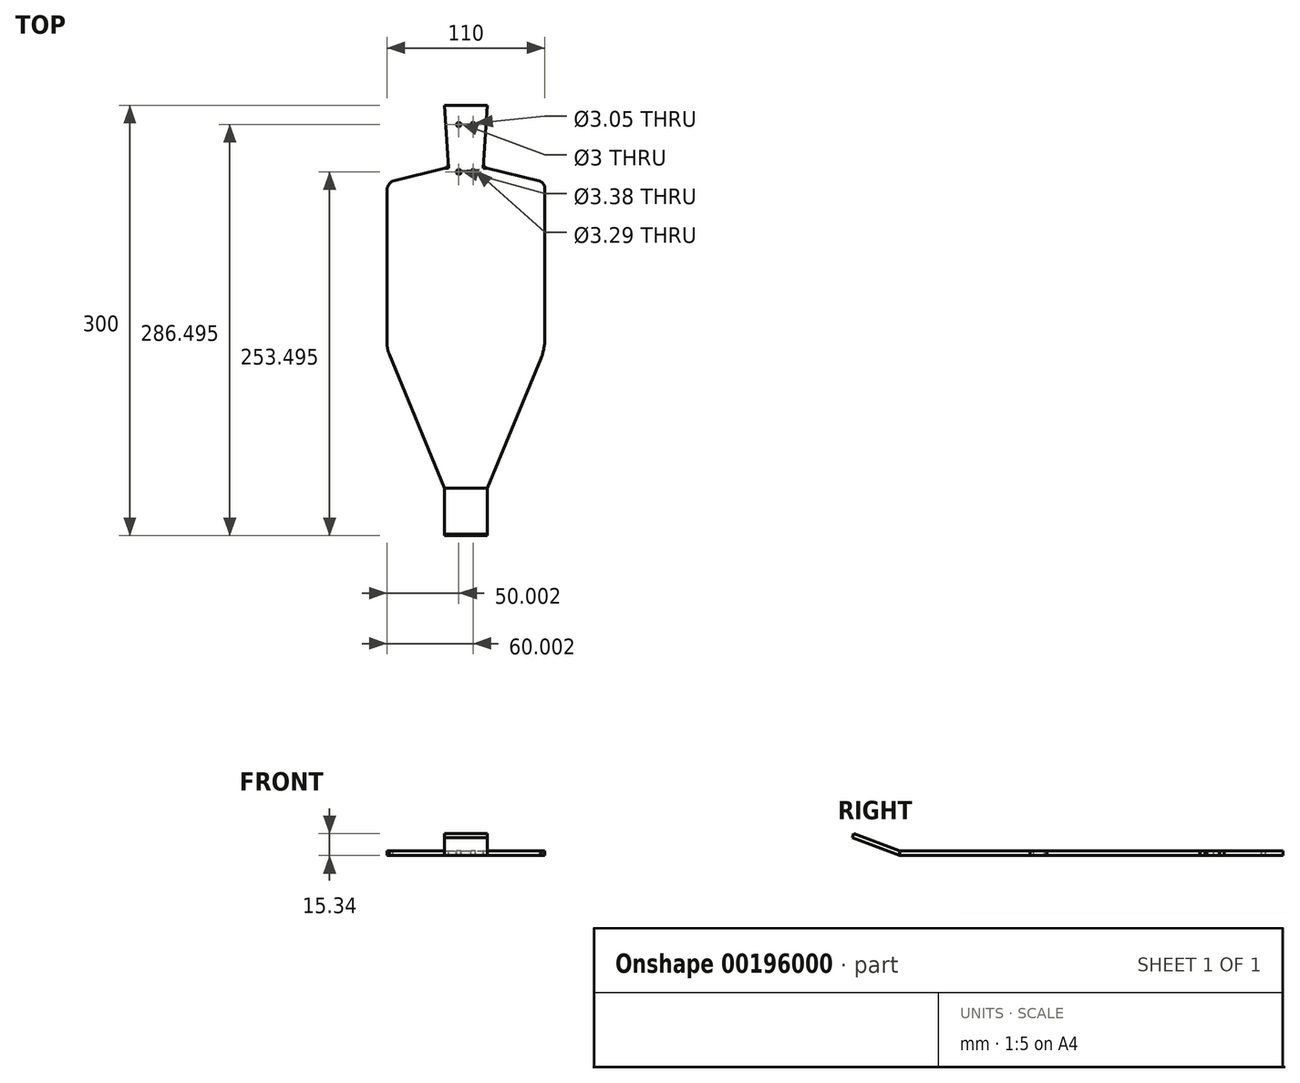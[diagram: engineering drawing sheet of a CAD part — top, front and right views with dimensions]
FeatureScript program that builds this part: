
annotation { "Feature Type Name" : "Feature", "Feature Type Description" : "" }
export const myFeature = defineFeature(function(context is Context, id is Id, definition is map)
    precondition{}
    {
        {
            var Q0;
            Q0=qCreatedBy(makeId("Top.planeOp"),FACE);
            var sketch = newSketch(context, id + "F0", { "sketchPlane" : qUnion([Q0])});
            skLineSegment(sketch, "E0.bottom", {"start": v(-49.3, 160.69) * mm, "end": v(-19.3, 160.69) * mm});
            skLineSegment(sketch, "E0.top", {"start": v(-49.3, -139.31) * mm, "end": v(-19.3, -139.31) * mm});
            skLineSegment(sketch, "E0.left", {"start": v(-49.3, -106.28) * mm, "end": v(-49.3, -139.31) * mm});
            skLineSegment(sketch, "E0.right", {"start": v(-19.3, -106.28) * mm, "end": v(-19.3, -139.31) * mm});
            skLineSegment(sketch, "E1", {"start": v(-49.3, 116.69) * mm, "end": v(-19.3, 116.69) * mm});
            skLineSegment(sketch, "E2", {"start": v(-19.3, 160.69) * mm, "end": v(-22.3, 116.69) * mm});
            skLineSegment(sketch, "E3", {"start": v(-46.3, 116.69) * mm, "end": v(-49.3, 116.69) * mm});
            skLineSegment(sketch, "E4", {"start": v(-49.3, 160.69) * mm, "end": v(-46.3, 116.69) * mm});
            skLineSegment(sketch, "E5", {"start": v(-49.3, 116.69) * mm, "end": v(-46.3, 116.69) * mm});
            skLineSegment(sketch, "E6", {"start": v(-49.3, 116.69) * mm, "end": v(-89.3, 106.83) * mm});
            skLineSegment(sketch, "E7", {"start": v(-19.3, 116.69) * mm, "end": v(20.7, 106.83) * mm});
            skLineSegment(sketch, "E8.left", {"start": v(-89.3, 106.83) * mm, "end": v(-89.3, -9.31) * mm});
            skLineSegment(sketch, "E8.right", {"start": v(20.7, 106.83) * mm, "end": v(20.7, -9.31) * mm});
            skLineSegment(sketch, "E9", {"start": v(-89.3, -9.31) * mm, "end": v(-49.3, -106.28) * mm});
            skLineSegment(sketch, "E10", {"start": v(-49.3, -106.28) * mm, "end": v(-19.3, -106.28) * mm});
            skLineSegment(sketch, "E11", {"start": v(-19.3, -106.28) * mm, "end": v(20.7, -9.31) * mm});
            skLineSegment(sketch, "E12.trimOffspring", {"start": v(-22.3, 116.69) * mm, "end": v(-19.3, 116.69) * mm});
            skPoint(sketch, "E13.orphan", {"position": v(-34.3, 160.69) * mm});
            skSolve(sketch);
        }
        {
            var Q0;
            Q0 = qSketchRegion(id + "F0", true);
            extrude(context, id + "F1", {"entities" : qUnion([Q0]), "depth" : 3.25 * mm});
        }
        {
            var Q0;
            Q0=makeQuery(id+"F0.imprint","IMPRINT",FACE,{"disambiguationData":[TD([[makeQuery(id+"F0.imprint","IMPRINT",EDGE,{"derivedFrom":sQuery(id+"F0.wireOp",EDGE,"E0.top")}),1.0]])]});
            extrude(context, id + "F2", {"entities" : qUnion([Q0]), "operationType" : NewBodyOperationType.ADD, "depth" : 25 * mm});
        }
        {
            var Q0;
            {var subQ0=sQuery(id+"F0.wireOp",EDGE,"E0.left");Q0=makeQuery(id+"F2.boolean.opBoolean","MERGE",FACE,{"derivedFrom":[makeQuery(id+"F1.opExtrude","SWEPT_FACE",FACE,{"disambiguationData":[OSD([subQ0])]}),makeQuery(id+"F2.opExtrude","SWEPT_FACE",FACE,{"disambiguationData":[OSD([subQ0])]})]});}
            var sketch = newSketch(context, id + "F3", { "sketchPlane" : qUnion([Q0])});
            skLineSegment(sketch, "E14", {"start": v(106.28, 3.25) * mm, "end": v(138.24, 15.34) * mm});
            skLineSegment(sketch, "E15", {"start": v(106.28, 0) * mm, "end": v(139.31, 12.5) * mm});
            skLineSegment(sketch, "E16", {"start": v(139.31, 12.5) * mm, "end": v(138.08, 15.75) * mm});
            skPoint(sketch, "E17.orphan", {"position": v(139.31, 15.75) * mm});
            skSolve(sketch);
        }
        {
            var Q0;
            Q0 = qSketchRegion(id + "F3", true);
            var Q1;
            {var subQ2=sQuery(id+"F3.wireOp",EDGE,"E14");Q1=makeQuery(id+"F3.imprint","IMPRINT",FACE,{"disambiguationData":[TD([[makeQuery(id+"F3.imprint","IMPRINT",EDGE,{"derivedFrom":subQ2}),1.0]])]});}
            var Q2;
            {var subQ0=sQuery(id+"F3.wireOp",EDGE,"E15");Q2=makeQuery(id+"F3.imprint","IMPRINT",FACE,{"disambiguationData":[TD([[makeQuery(id+"F3.imprint","IMPRINT",EDGE,{"derivedFrom":subQ0}),-1.0]])]});}
            extrude(context, id + "F4", {"entities" : qUnion([Q0, Q1, Q2]), "operationType" : NewBodyOperationType.REMOVE, "oppositeDirection" : true, "depth" : 70 * mm});
        }
        {
            var Q0;
            Q0=makeQuery(id+"F1.opExtrude","CAP_FACE",FACE,{"disambiguationData":[OSD([sQuery(id+"F0.wireOp",EDGE,"E0.bottom"),sQuery(id+"F0.wireOp",EDGE,"E0.top"),sQuery(id+"F0.wireOp",EDGE,"E0.left"),sQuery(id+"F0.wireOp",EDGE,"E0.right"),sQuery(id+"F0.wireOp",EDGE,"E2"),sQuery(id+"F0.wireOp",EDGE,"E4"),sQuery(id+"F0.wireOp",EDGE,"E5"),sQuery(id+"F0.wireOp",EDGE,"E6"),sQuery(id+"F0.wireOp",EDGE,"E7"),sQuery(id+"F0.wireOp",EDGE,"E8.left"),sQuery(id+"F0.wireOp",EDGE,"E8.right"),sQuery(id+"F0.wireOp",EDGE,"E9"),sQuery(id+"F0.wireOp",EDGE,"E11"),sQuery(id+"F0.wireOp",EDGE,"E12.trimOffspring")])],"isStart":false});
            var sketch = newSketch(context, id + "F5", { "sketchPlane" : qUnion([Q0])});
            skArc(sketch, "E18", {"start": v(-89.3, -3.58) * mm, "mid": v(-89.01, -8.32) * mm, "end": v(-87.81, -12.92) * mm});
            skArc(sketch, "E19", {"start": v(18.14, -15.52) * mm, "mid": v(19.8, -9.63) * mm, "end": v(20.7, -3.58) * mm});
            skSolve(sketch);
        }
        {
            var Q0;
            {var subQ0=sQuery(id+"F5.wireOp",EDGE,"E19");Q0=makeQuery(id+"F5.imprint","IMPRINT",FACE,{"disambiguationData":[TD([[makeQuery(id+"F5.imprint","IMPRINT",EDGE,{"derivedFrom":subQ0}),-1.0]])]});}
            var Q1;
            {var subQ0=sQuery(id+"F5.wireOp",EDGE,"E18");var subQ1=makeQuery(id+"F1.opExtrude","CAP_EDGE",EDGE,{"disambiguationData":[OSD([sQuery(id+"F0.wireOp",EDGE,"E9")])],"isStart":false});var subQ2=makeQuery(id+"F5.imprint","INTERSECT",VERTEX,{"derivedFrom":[subQ1,subQ0]});Q1=makeQuery(id+"F5.imprint","IMPRINT",FACE,{"disambiguationData":[TD([[makeQuery(id+"F5.imprint","IMPRINT",EDGE,{"disambiguationData":[TD([[subQ2,1.0]])],"derivedFrom":subQ0}),-1.0]])]});}
            extrude(context, id + "F6", {"entities" : qUnion([Q0, Q1]), "operationType" : NewBodyOperationType.REMOVE, "oppositeDirection" : true, "depth" : 25 * mm});
        }
        {
            var Q0;
            Q0=makeQuery(id+"F1.opExtrude","CAP_FACE",FACE,{"disambiguationData":[OSD([sQuery(id+"F0.wireOp",EDGE,"E0.bottom"),sQuery(id+"F0.wireOp",EDGE,"E0.top"),sQuery(id+"F0.wireOp",EDGE,"E0.left"),sQuery(id+"F0.wireOp",EDGE,"E0.right"),sQuery(id+"F0.wireOp",EDGE,"E2"),sQuery(id+"F0.wireOp",EDGE,"E4"),sQuery(id+"F0.wireOp",EDGE,"E5"),sQuery(id+"F0.wireOp",EDGE,"E6"),sQuery(id+"F0.wireOp",EDGE,"E7"),sQuery(id+"F0.wireOp",EDGE,"E8.left"),sQuery(id+"F0.wireOp",EDGE,"E8.right"),sQuery(id+"F0.wireOp",EDGE,"E9"),sQuery(id+"F0.wireOp",EDGE,"E11"),sQuery(id+"F0.wireOp",EDGE,"E12.trimOffspring")])],"isStart":false});
            var sketch = newSketch(context, id + "F7", { "sketchPlane" : qUnion([Q0])});
            skArc(sketch, "E20", {"start": v(20.7, 103.06) * mm, "mid": v(19.86, 105.53) * mm, "end": v(18.12, 107.47) * mm});
            skArc(sketch, "E21", {"start": v(-85.14, 107.86) * mm, "mid": v(-87.8, 105.58) * mm, "end": v(-89.3, 102.4) * mm});
            skSolve(sketch);
        }
        {
            var Q0;
            Q0 = qSketchRegion(id + "F7", true);
            var Q1;
            {var subQ0=sQuery(id+"F7.wireOp",EDGE,"E21");Q1=makeQuery(id+"F7.imprint","IMPRINT",FACE,{"disambiguationData":[TD([[makeQuery(id+"F7.imprint","IMPRINT",EDGE,{"derivedFrom":subQ0}),-1.0]])]});}
            var Q2;
            {var subQ0=sQuery(id+"F7.wireOp",EDGE,"E20");Q2=makeQuery(id+"F7.imprint","IMPRINT",FACE,{"disambiguationData":[TD([[makeQuery(id+"F7.imprint","IMPRINT",EDGE,{"derivedFrom":subQ0}),-1.0]])]});}
            extrude(context, id + "F8", {"entities" : qUnion([Q0, Q1, Q2]), "operationType" : NewBodyOperationType.REMOVE, "oppositeDirection" : true, "depth" : 25 * mm});
        }
        {
            var Q0;
            Q0=makeQuery(id+"F1.opExtrude","CAP_FACE",FACE,{"disambiguationData":[OSD([sQuery(id+"F0.wireOp",EDGE,"E0.bottom"),sQuery(id+"F0.wireOp",EDGE,"E0.top"),sQuery(id+"F0.wireOp",EDGE,"E0.left"),sQuery(id+"F0.wireOp",EDGE,"E0.right"),sQuery(id+"F0.wireOp",EDGE,"E2"),sQuery(id+"F0.wireOp",EDGE,"E4"),sQuery(id+"F0.wireOp",EDGE,"E5"),sQuery(id+"F0.wireOp",EDGE,"E6"),sQuery(id+"F0.wireOp",EDGE,"E7"),sQuery(id+"F0.wireOp",EDGE,"E8.left"),sQuery(id+"F0.wireOp",EDGE,"E8.right"),sQuery(id+"F0.wireOp",EDGE,"E9"),sQuery(id+"F0.wireOp",EDGE,"E11"),sQuery(id+"F0.wireOp",EDGE,"E12.trimOffspring")])],"isStart":false});
            var sketch = newSketch(context, id + "F9", { "sketchPlane" : qUnion([Q0])});
            skArc(sketch, "E22", {"start": v(19.14, 106.52) * mm, "mid": v(18.14, 107.27) * mm, "end": v(16.98, 107.75) * mm});
            skSolve(sketch);
        }
        {
            var Q0;
            Q0 = qSketchRegion(id + "F9", true);
            var Q1;
            {var subQ0=sQuery(id+"F9.wireOp",EDGE,"E22");Q1=makeQuery(id+"F9.imprint","IMPRINT",FACE,{"disambiguationData":[TD([[makeQuery(id+"F9.imprint","IMPRINT",EDGE,{"derivedFrom":subQ0}),-1.0]])]});}
            extrude(context, id + "F10", {"entities" : qUnion([Q0, Q1]), "operationType" : NewBodyOperationType.REMOVE, "oppositeDirection" : true, "depth" : 25 * mm});
        }
        {
            var Q0;
            Q0=makeQuery(id+"F1.opExtrude","CAP_FACE",FACE,{"disambiguationData":[OSD([sQuery(id+"F0.wireOp",EDGE,"E0.bottom"),sQuery(id+"F0.wireOp",EDGE,"E0.top"),sQuery(id+"F0.wireOp",EDGE,"E0.left"),sQuery(id+"F0.wireOp",EDGE,"E0.right"),sQuery(id+"F0.wireOp",EDGE,"E2"),sQuery(id+"F0.wireOp",EDGE,"E4"),sQuery(id+"F0.wireOp",EDGE,"E5"),sQuery(id+"F0.wireOp",EDGE,"E6"),sQuery(id+"F0.wireOp",EDGE,"E7"),sQuery(id+"F0.wireOp",EDGE,"E8.left"),sQuery(id+"F0.wireOp",EDGE,"E8.right"),sQuery(id+"F0.wireOp",EDGE,"E9"),sQuery(id+"F0.wireOp",EDGE,"E11"),sQuery(id+"F0.wireOp",EDGE,"E12.trimOffspring")])],"isStart":false});
            var sketch = newSketch(context, id + "F11", { "sketchPlane" : qUnion([Q0])});
            skArc(sketch, "E23", {"start": v(-49.3, 116.69) * mm, "mid": v(-47.46, 117.75) * mm, "end": v(-46.5, 119.64) * mm});
            skArc(sketch, "E24", {"start": v(-22.1, 119.64) * mm, "mid": v(-21.13, 117.75) * mm, "end": v(-19.3, 116.69) * mm});
            skSolve(sketch);
        }
        {
            var Q0;
            Q0 = qSketchRegion(id + "F11", true);
            var Q1;
            {var subQ0=sQuery(id+"F11.wireOp",EDGE,"E23");Q1=makeQuery(id+"F11.imprint","IMPRINT",FACE,{"disambiguationData":[TD([[makeQuery(id+"F11.imprint","IMPRINT",EDGE,{"derivedFrom":subQ0}),-1.0]])]});}
            var Q2;
            {var subQ0=sQuery(id+"F11.wireOp",EDGE,"E24");Q2=makeQuery(id+"F11.imprint","IMPRINT",FACE,{"disambiguationData":[TD([[makeQuery(id+"F11.imprint","IMPRINT",EDGE,{"derivedFrom":subQ0}),-1.0]])]});}
            extrude(context, id + "F12", {"entities" : qUnion([Q0, Q1, Q2]), "oppositeDirection" : true, "depth" : 3.25 * mm});
        }
        {
            var Q0;
            Q0=makeQuery(id+"F1.opExtrude","CAP_FACE",FACE,{"disambiguationData":[OSD([sQuery(id+"F0.wireOp",EDGE,"E0.bottom"),sQuery(id+"F0.wireOp",EDGE,"E0.top"),sQuery(id+"F0.wireOp",EDGE,"E0.left"),sQuery(id+"F0.wireOp",EDGE,"E0.right"),sQuery(id+"F0.wireOp",EDGE,"E2"),sQuery(id+"F0.wireOp",EDGE,"E4"),sQuery(id+"F0.wireOp",EDGE,"E5"),sQuery(id+"F0.wireOp",EDGE,"E6"),sQuery(id+"F0.wireOp",EDGE,"E7"),sQuery(id+"F0.wireOp",EDGE,"E8.left"),sQuery(id+"F0.wireOp",EDGE,"E8.right"),sQuery(id+"F0.wireOp",EDGE,"E9"),sQuery(id+"F0.wireOp",EDGE,"E11"),sQuery(id+"F0.wireOp",EDGE,"E12.trimOffspring")])],"isStart":false});
            var sketch = newSketch(context, id + "F13", { "sketchPlane" : qUnion([Q0])});
            skLineSegment(sketch, "E25", {"start": v(-34.3, 160.69) * mm, "end": v(-34.3, 107.56) * mm});
            skCircle(sketch, "E26", {"center": v(-39.3, 147.19) * mm, "radius": 1.5 * mm});
            skCircle(sketch, "E27", {"center": v(-29.3, 147.19) * mm, "radius": 1.53 * mm});
            skCircle(sketch, "E28", {"center": v(-39.3, 114.19) * mm, "radius": 1.69 * mm});
            skCircle(sketch, "E29", {"center": v(-29.3, 114.19) * mm, "radius": 1.64 * mm});
            skSolve(sketch);
        }
        {
            var Q0;
            Q0=makeQuery(id+"F13.imprint","IMPRINT",FACE,{"disambiguationData":[TD([[makeQuery(id+"F13.imprint","IMPRINT",EDGE,{"derivedFrom":sQuery(id+"F13.wireOp",EDGE,"E27")}),1.0]])]});
            var Q1;
            Q1=makeQuery(id+"F13.imprint","IMPRINT",FACE,{"disambiguationData":[TD([[makeQuery(id+"F13.imprint","IMPRINT",EDGE,{"derivedFrom":sQuery(id+"F13.wireOp",EDGE,"E26")}),1.0]])]});
            var Q2;
            Q2=makeQuery(id+"F13.imprint","IMPRINT",FACE,{"disambiguationData":[TD([[makeQuery(id+"F13.imprint","IMPRINT",EDGE,{"derivedFrom":sQuery(id+"F13.wireOp",EDGE,"E28")}),1.0]])]});
            var Q3;
            Q3=makeQuery(id+"F13.imprint","IMPRINT",FACE,{"disambiguationData":[TD([[makeQuery(id+"F13.imprint","IMPRINT",EDGE,{"derivedFrom":sQuery(id+"F13.wireOp",EDGE,"E29")}),1.0]])]});
            extrude(context, id + "F14", {"entities" : qUnion([Q0, Q1, Q2, Q3]), "operationType" : NewBodyOperationType.REMOVE, "oppositeDirection" : true, "depth" : 25 * mm});
        }
    });
